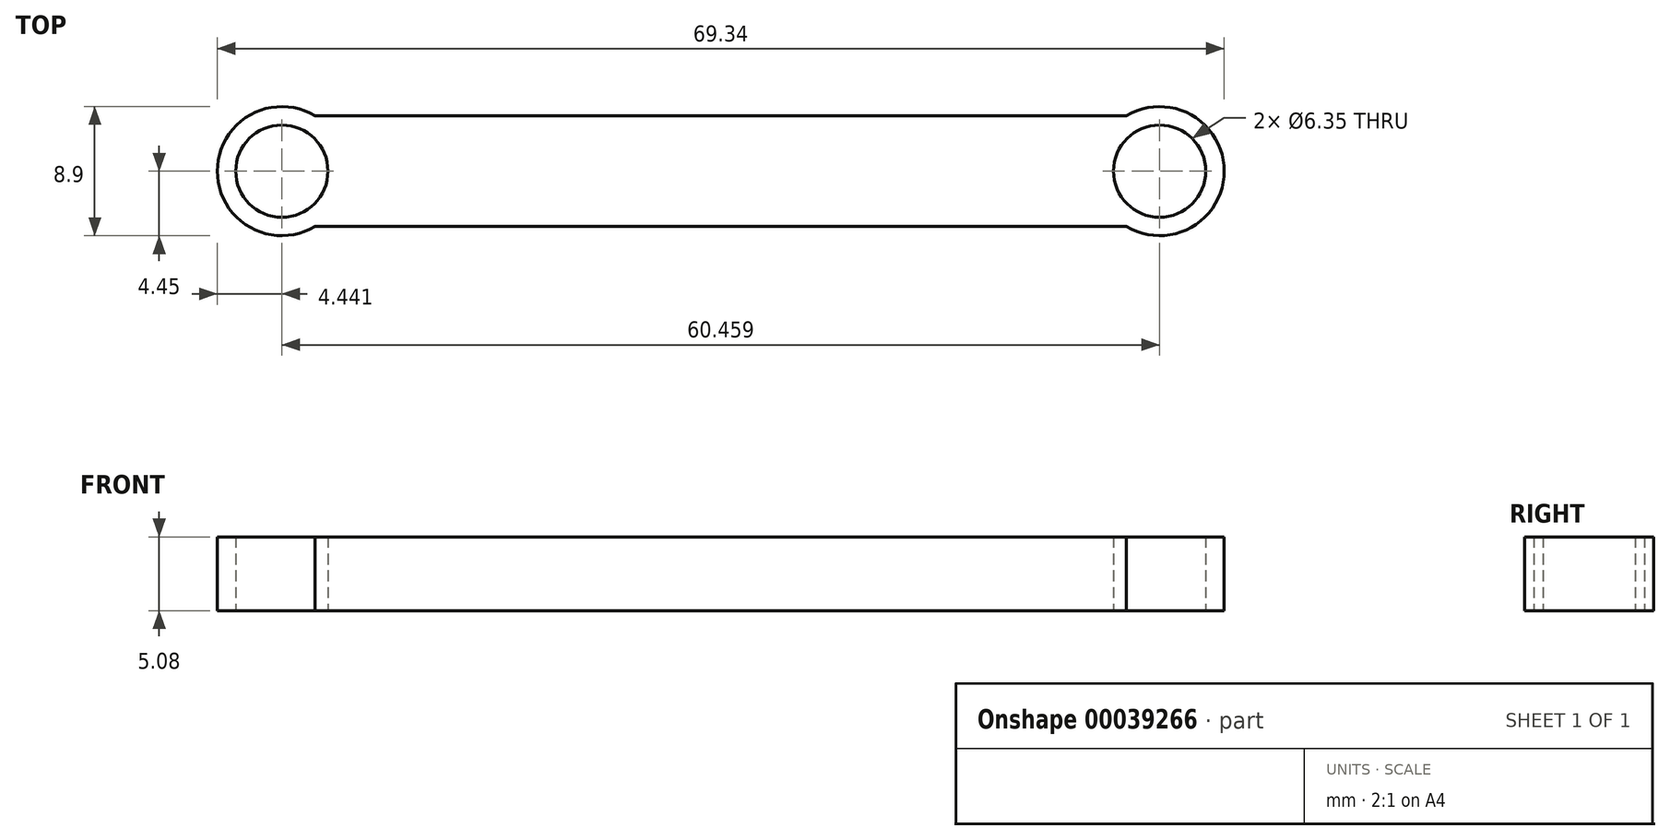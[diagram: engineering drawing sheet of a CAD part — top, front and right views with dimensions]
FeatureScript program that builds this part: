
annotation { "Feature Type Name" : "Feature", "Feature Type Description" : "" }
export const myFeature = defineFeature(function(context is Context, id is Id, definition is map)
    precondition{}
    {
        {
            var Q0;
            Q0=qCreatedBy(makeId("Top.planeOp"),FACE);
            var sketch = newSketch(context, id + "F0", { "sketchPlane" : qUnion([Q0])});
            skLineSegment(sketch, "E0.rect.bottom", {"start": v(27.94, 3.8) * mm, "end": v(-27.94, 3.8) * mm});
            skLineSegment(sketch, "E0.rect.top", {"start": v(27.94, -3.81) * mm, "end": v(-27.94, -3.81) * mm});
            skPoint(sketch, "E0.rect.middle", {"position": v(0, 0) * mm});
            skCircle(sketch, "E1", {"center": v(-30.23, 0) * mm, "radius": 3.18 * mm});
            skCircle(sketch, "E2", {"center": v(30.23, 0) * mm, "radius": 3.17 * mm});
            skCircle(sketch, "E3", {"center": v(30.23, 0) * mm, "radius": 4.45 * mm});
            skCircle(sketch, "E4", {"center": v(-30.23, 0) * mm, "radius": 4.45 * mm});
            skPoint(sketch, "E5.orphan", {"position": v(-30.23, 3.8) * mm});
            skPoint(sketch, "E6.orphan", {"position": v(-30.23, -3.81) * mm});
            skPoint(sketch, "E0.rect.left.start.orphan", {"position": v(30.23, 3.8) * mm});
            skPoint(sketch, "E7.trimOffspring.end.orphan", {"position": v(30.23, -3.81) * mm});
            skSolve(sketch);
        }
        {
            var Q0;
            Q0 = qSketchRegion(id + "F0", true);
            extrude(context, id + "F1", {"entities" : qUnion([Q0]), "depth" : 5.08 * mm});
        }
    });
